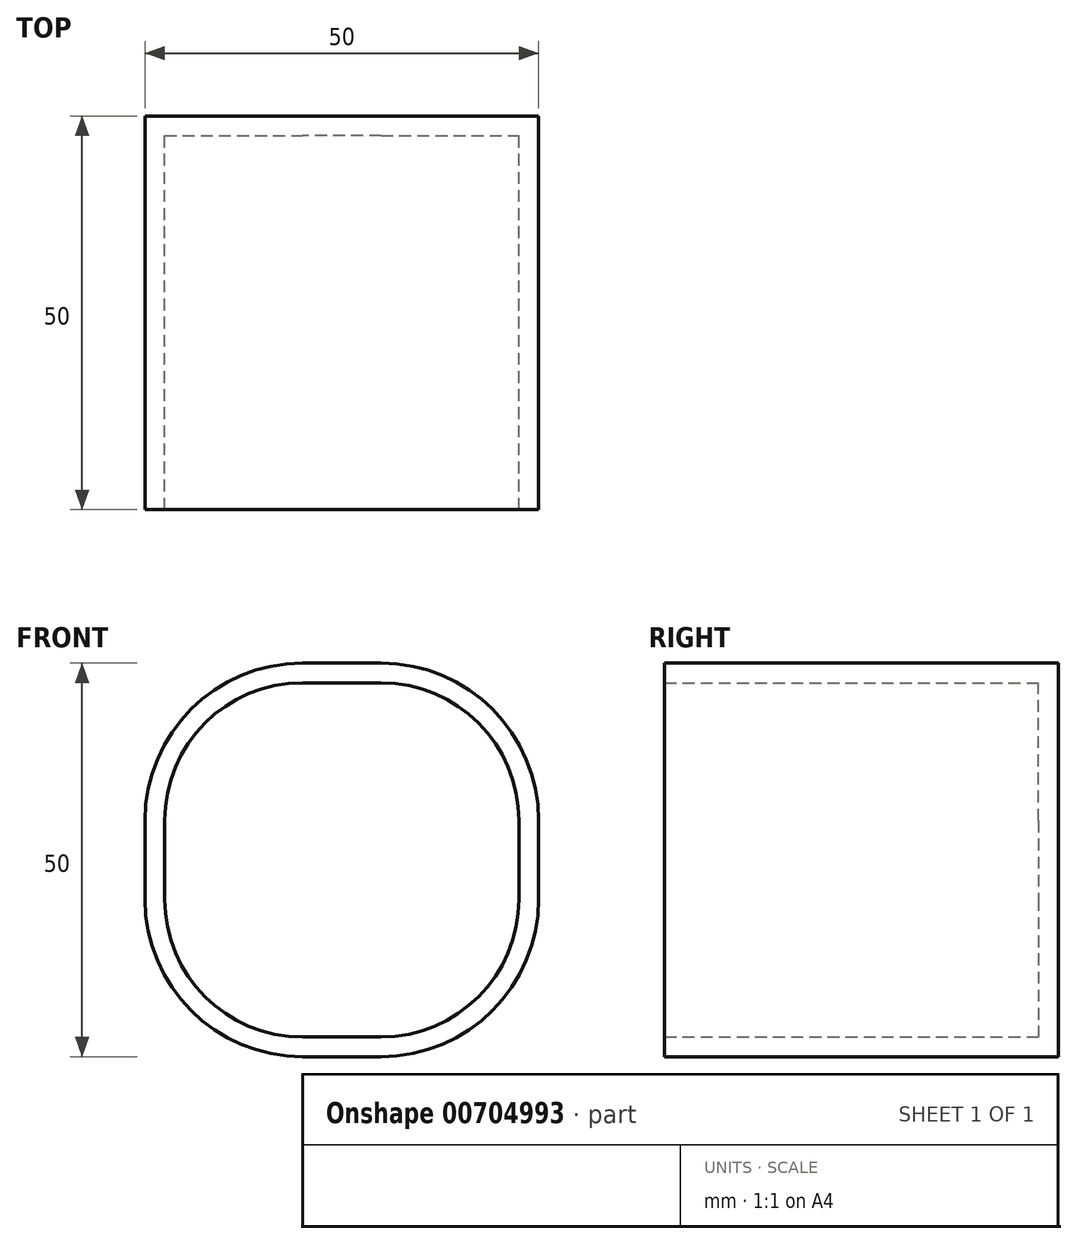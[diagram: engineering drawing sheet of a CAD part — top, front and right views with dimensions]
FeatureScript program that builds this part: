
annotation { "Feature Type Name" : "Feature", "Feature Type Description" : "" }
export const myFeature = defineFeature(function(context is Context, id is Id, definition is map)
    precondition{}
    {
        {
            var Q0;
            Q0=qCreatedBy(makeId("Top.planeOp"),FACE);
            var sketch = newSketch(context, id + "F0", { "sketchPlane" : qUnion([Q0])});
            skPoint(sketch, "E0.middle", {"position": v(0, 0) * mm});
            skLineSegment(sketch, "E1.bottom", {"start": v(25, -23.4) * mm, "end": v(-25, -23.4) * mm});
            skLineSegment(sketch, "E1.top", {"start": v(25, 26.6) * mm, "end": v(-25, 26.6) * mm});
            skLineSegment(sketch, "E1.left", {"start": v(25, -23.4) * mm, "end": v(25, 26.6) * mm});
            skLineSegment(sketch, "E1.right", {"start": v(-25, -23.4) * mm, "end": v(-25, 26.6) * mm});
            skPoint(sketch, "E1.middle", {"position": v(0, 1.6) * mm});
            skSolve(sketch);
        }
        {
            var Q0;
            Q0=makeQuery(id+"F0.imprint","IMPRINT",FACE,{"disambiguationData":[TD([[makeQuery(id+"F0.imprint","IMPRINT",EDGE,{"derivedFrom":sQuery(id+"F0.wireOp",EDGE,"E1.bottom")}),-1.0]])]});
            extrude(context, id + "F1", {"entities" : qUnion([Q0]), "depth" : 50 * mm, "offsetDistance" : 25 * mm});
        }
        {
            var Q0;
            Q0=makeQuery(id+"F1.opExtrude","CAP_EDGE",EDGE,{"disambiguationData":[OSD([sQuery(id+"F0.wireOp",EDGE,"E1.left")])],"isStart":true});
            var Q1;
            Q1=makeQuery(id+"F1.opExtrude","CAP_EDGE",EDGE,{"disambiguationData":[OSD([sQuery(id+"F0.wireOp",EDGE,"E1.right")])],"isStart":true});
            var Q2;
            Q2=makeQuery(id+"F1.opExtrude","CAP_EDGE",EDGE,{"disambiguationData":[OSD([sQuery(id+"F0.wireOp",EDGE,"E1.left")])],"isStart":false});
            var Q3;
            Q3=makeQuery(id+"F1.opExtrude","CAP_EDGE",EDGE,{"disambiguationData":[OSD([sQuery(id+"F0.wireOp",EDGE,"E1.right")])],"isStart":false});
            fillet(context, id + "F2", {"entities" : qUnion([Q0, Q1, Q2, Q3]), "radius" : 20 * mm, "tangentPropagation" : true, "allowEdgeOverflow" : false});
        }
        {
            var Q0;
            Q0=makeQuery(id+"F1.opExtrude","SWEPT_FACE",FACE,{"disambiguationData":[OSD([sQuery(id+"F0.wireOp",EDGE,"E1.bottom")])]});
            shell(context, id + "F3", {"entities" : qUnion([Q0]), "thickness" : 2.5 * mm});
        }
    });
